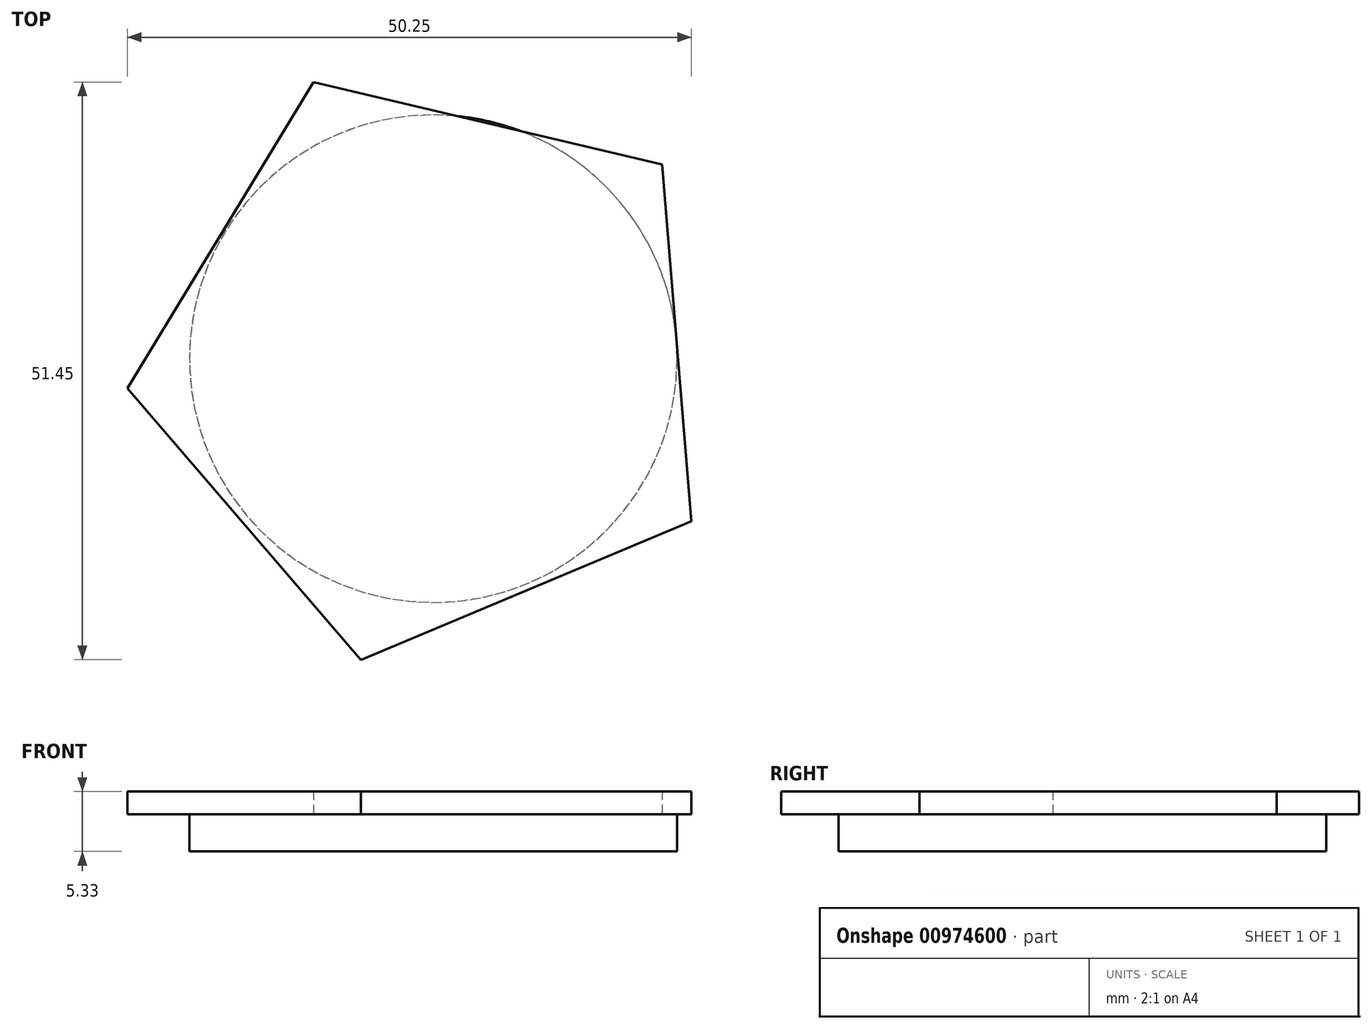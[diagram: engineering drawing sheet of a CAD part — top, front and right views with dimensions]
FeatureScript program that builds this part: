
annotation { "Feature Type Name" : "Feature", "Feature Type Description" : "" }
export const myFeature = defineFeature(function(context is Context, id is Id, definition is map)
    precondition{}
    {
        {
            var Q0;
            Q0=qCreatedBy(makeId("Top.planeOp"),FACE);
            var sketch = newSketch(context, id + "F0", { "sketchPlane" : qUnion([Q0])});
            skCircle(sketch, "E0.cCircle", {"center": v(-40.56, 19.07) * mm, "radius": 21.96 * mm, "construction": true});
            skLineSegment(sketch, "E0.0", {"start": v(-19.99, 36.78) * mm, "end": v(-17.36, 4.98) * mm});
            skLineSegment(sketch, "E0.1", {"start": v(-17.36, 4.98) * mm, "end": v(-46.8, -7.34) * mm});
            skLineSegment(sketch, "E0.2", {"start": v(-46.8, -7.34) * mm, "end": v(-67.6, 16.84) * mm});
            skLineSegment(sketch, "E0.3", {"start": v(-67.6, 16.84) * mm, "end": v(-51.04, 44.11) * mm});
            skLineSegment(sketch, "E0.4", {"start": v(-51.04, 44.11) * mm, "end": v(-19.99, 36.78) * mm});
            skPoint(sketch, "E0.0.midPoint", {"position": v(-18.67, 20.88) * mm});
            skSolve(sketch);
        }
        {
            var Q0;
            Q0=qCreatedBy(makeId("Top.planeOp"),FACE);
            var sketch = newSketch(context, id + "F1", { "sketchPlane" : qUnion([Q0])});
            skCircle(sketch, "E1", {"center": v(-40.36, 19.48) * mm, "radius": 21.72 * mm});
            skSolve(sketch);
        }
        {
            var Q0;
            Q0=makeQuery(id+"F0.imprint","IMPRINT",FACE,{"disambiguationData":[TD([[makeQuery(id+"F0.imprint","IMPRINT",EDGE,{"derivedFrom":sQuery(id+"F0.wireOp",EDGE,"E0.0")}),-1.0]])]});
            extrude(context, id + "F2", {"entities" : qUnion([Q0]), "depth" : 2.03 * mm, "offsetDistance" : 25.4 * mm});
        }
        {
            var Q0;
            Q0=makeQuery(id+"F1.imprint","IMPRINT",FACE,{"disambiguationData":[TD([[makeQuery(id+"F1.imprint","IMPRINT",EDGE,{"derivedFrom":sQuery(id+"F1.wireOp",EDGE,"E1")}),1.0]])]});
            extrude(context, id + "F3", {"entities" : qUnion([Q0]), "operationType" : NewBodyOperationType.ADD, "oppositeDirection" : true, "depth" : 3.3 * mm, "offsetDistance" : 25.4 * mm});
        }
    });
